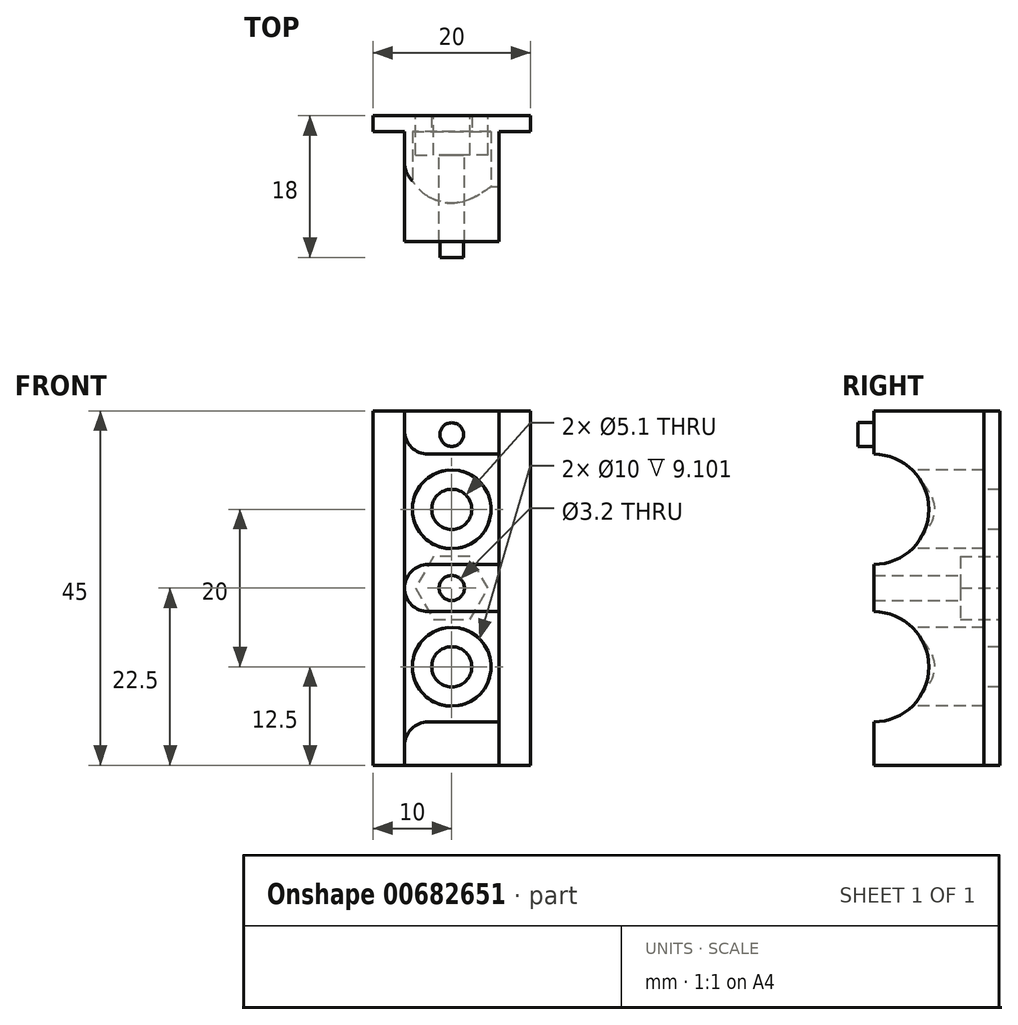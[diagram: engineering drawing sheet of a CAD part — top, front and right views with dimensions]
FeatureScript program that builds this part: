
annotation { "Feature Type Name" : "Feature", "Feature Type Description" : "" }
export const myFeature = defineFeature(function(context is Context, id is Id, definition is map)
    precondition{}
    {
        {
            var Q0;
            Q0=qCreatedBy(makeId("Front.planeOp"),FACE);
            cPlane(context, id + "F0", {"entities" : qUnion([Q0]), "cplaneType" : CPlaneType.OFFSET, "offset" : 16 * mm, "width" : 150 * mm, "height" : 150 * mm});
        }
        {
            var Q0;
            Q0=qCreatedBy(makeId("Front.planeOp"),FACE);
            var sketch = newSketch(context, id + "F1", { "sketchPlane" : qUnion([Q0])});
            skLineSegment(sketch, "E0.bottom", {"start": v(-6, 22.5) * mm, "end": v(6, 22.5) * mm});
            skLineSegment(sketch, "E0.top", {"start": v(-6, -22.5) * mm, "end": v(6, -22.5) * mm});
            skLineSegment(sketch, "E0.left", {"start": v(-6, 22.5) * mm, "end": v(-6, -22.5) * mm});
            skLineSegment(sketch, "E0.right", {"start": v(6, 22.5) * mm, "end": v(6, -22.5) * mm});
            skSolve(sketch);
        }
        {
            var Q0;
            Q0=qSketchRegion(id+"F1",true);
            extrude(context, id + "F2", {"entities" : qUnion([Q0]), "depth" : 30 * mm, "offsetDistance" : 25 * mm});
        }
        {
            var Q0;
            Q0=makeQuery(id+"F2.opExtrude","SWEPT_FACE",FACE,{"disambiguationData":[OSD([sQuery(id+"F1.wireOp",EDGE,"E0.right")])]});
            var sketch = newSketch(context, id + "F3", { "sketchPlane" : qUnion([Q0])});
            skCircle(sketch, "E1", {"center": v(-16, 10) * mm, "radius": 7 * mm});
            skCircle(sketch, "E2", {"center": v(-16, -10) * mm, "radius": 7 * mm});
            skSolve(sketch);
        }
        {
            var Q0;
            Q0=qSketchRegion(id+"F3",true);
            extrude(context, id + "F4", {"entities" : qUnion([Q0]), "operationType" : NewBodyOperationType.REMOVE, "endBound" : BoundingType.THROUGH_ALL, "oppositeDirection" : true, "depth" : 25 * mm, "offsetDistance" : 25 * mm});
        }
        {
            var Q0;
            Q0=qCreatedBy(makeId("Front.planeOp"),FACE);
            var sketch = newSketch(context, id + "F5", { "sketchPlane" : qUnion([Q0])});
            skLineSegment(sketch, "E3.bottom", {"start": v(-10, 22.5) * mm, "end": v(10, 22.5) * mm});
            skLineSegment(sketch, "E3.top", {"start": v(-10, -22.5) * mm, "end": v(10, -22.5) * mm});
            skLineSegment(sketch, "E3.left", {"start": v(-10, 22.5) * mm, "end": v(-10, -22.5) * mm});
            skLineSegment(sketch, "E3.right", {"start": v(10, 22.5) * mm, "end": v(10, -22.5) * mm});
            skPoint(sketch, "E4", {"position": v(0, 22.5) * mm});
            skSolve(sketch);
        }
        {
            var Q0;
            Q0=qSketchRegion(id+"F5",true);
            extrude(context, id + "F6", {"entities" : qUnion([Q0]), "operationType" : NewBodyOperationType.ADD, "depth" : 2 * mm, "offsetDistance" : 25 * mm});
        }
        {
            var Q0;
            Q0=makeQuery(id+"F4.boolean.opBoolean","INTERSECT",EDGE,{"derivedFrom":[makeQuery(id+"F2.opExtrude","SWEPT_FACE",FACE,{"disambiguationData":[OSD([sQuery(id+"F1.wireOp",EDGE,"E0.left")])]}),makeQuery(id+"F4.opExtrude","SWEPT_FACE",FACE,{"disambiguationData":[OSD([sQuery(id+"F3.wireOp",EDGE,"E1")])]})]});
            var Q1;
            Q1=makeQuery(id+"F4.boolean.opBoolean","INTERSECT",EDGE,{"derivedFrom":[makeQuery(id+"F2.opExtrude","SWEPT_FACE",FACE,{"disambiguationData":[OSD([sQuery(id+"F1.wireOp",EDGE,"E0.left")])]}),makeQuery(id+"F4.opExtrude","SWEPT_FACE",FACE,{"disambiguationData":[OSD([sQuery(id+"F3.wireOp",EDGE,"E2")])]})]});
            var Q2;
            Q2=makeQuery(id+"F4.boolean.opBoolean","COPY",EDGE,{"derivedFrom":makeQuery(id+"F4.opExtrude","CAP_EDGE",EDGE,{"disambiguationData":[OSD([sQuery(id+"F3.wireOp",EDGE,"E1")])],"isStart":true})});
            var Q3;
            Q3=makeQuery(id+"F4.boolean.opBoolean","COPY",EDGE,{"derivedFrom":makeQuery(id+"F4.opExtrude","CAP_EDGE",EDGE,{"disambiguationData":[OSD([sQuery(id+"F3.wireOp",EDGE,"E2")])],"isStart":true})});
            fillet(context, id + "F7", {"entities" : qUnion([Q0, Q1, Q2, Q3]), "radius" : 3 * mm, "tangentPropagation" : true, "allowEdgeOverflow" : false});
        }
        {
            var Q0;
            Q0=makeQuery(id+"F6.boolean.opBoolean","MERGE",FACE,{"derivedFrom":[makeQuery(id+"F2.opExtrude","CAP_FACE",FACE,{"disambiguationData":[OSD([sQuery(id+"F1.wireOp",EDGE,"E0.bottom"),sQuery(id+"F1.wireOp",EDGE,"E0.top"),sQuery(id+"F1.wireOp",EDGE,"E0.left"),sQuery(id+"F1.wireOp",EDGE,"E0.right")])],"isStart":true}),makeQuery(id+"F6.opExtrude","CAP_FACE",FACE,{"disambiguationData":[OSD([sQuery(id+"F5.wireOp",EDGE,"E3.bottom"),sQuery(id+"F5.wireOp",EDGE,"E3.top"),sQuery(id+"F5.wireOp",EDGE,"E3.left"),sQuery(id+"F5.wireOp",EDGE,"E3.right")])],"isStart":true})]});
            var sketch = newSketch(context, id + "F8", { "sketchPlane" : qUnion([Q0])});
            skPoint(sketch, "E5", {"position": v(0, 10) * mm});
            skPoint(sketch, "E6", {"position": v(0, -10) * mm});
            skPoint(sketch, "E7", {"position": v(0, 0) * mm});
            skSolve(sketch);
        }
        {
            var Q0;
            Q0=sQuery(id+"F8.wireOp",VERTEX,"E5");
            var Q1;
            Q1=sQuery(id+"F8.wireOp",VERTEX,"E6");
            var Q2;
            Q2=sQuery(id+"F8.wireOp",VERTEX,"E7");
            var Q3;
            Q3=makeQuery(id+"F2.opExtrude","SWEPT_BODY",BODY,{"disambiguationData":[OSD([sQuery(id+"F1.wireOp",EDGE,"E0.bottom"),sQuery(id+"F1.wireOp",EDGE,"E0.top"),sQuery(id+"F1.wireOp",EDGE,"E0.left"),sQuery(id+"F1.wireOp",EDGE,"E0.right")])]});
            hole(context, id + "F9", {"style" : HoleStyle.SIMPLE, "endStyle" : HoleEndStyle.THROUGH, "holeDiameter" : 3.2 * mm, "majorDiameter" : 5 * mm, "isTappedThrough" : true, "tappedDepth" : 12 * mm, "tapClearance" : 3, "startFromSketch" : true, "locations" : qUnion([Q0, Q1, Q2]), "scope" : qUnion([Q3])});
        }
        {
            var Q0;
            Q0=makeQuery(id+"F6.boolean.opBoolean","MERGE",FACE,{"derivedFrom":[makeQuery(id+"F2.opExtrude","CAP_FACE",FACE,{"disambiguationData":[OSD([sQuery(id+"F1.wireOp",EDGE,"E0.bottom"),sQuery(id+"F1.wireOp",EDGE,"E0.top"),sQuery(id+"F1.wireOp",EDGE,"E0.left"),sQuery(id+"F1.wireOp",EDGE,"E0.right")])],"isStart":true}),makeQuery(id+"F6.opExtrude","CAP_FACE",FACE,{"disambiguationData":[OSD([sQuery(id+"F5.wireOp",EDGE,"E3.bottom"),sQuery(id+"F5.wireOp",EDGE,"E3.top"),sQuery(id+"F5.wireOp",EDGE,"E3.left"),sQuery(id+"F5.wireOp",EDGE,"E3.right")])],"isStart":true})]});
            var sketch = newSketch(context, id + "F10", { "sketchPlane" : qUnion([Q0])});
            skSolve(sketch);
        }
        {
            var Q0;
            Q0=makeQuery(id+"F2.opExtrude","CAP_EDGE",EDGE,{"disambiguationData":[OSD([sQuery(id+"F1.wireOp",EDGE,"E0.top")])],"isStart":false});
            var Q1;
            Q1=makeQuery(id+"F2.opExtrude","CAP_EDGE",EDGE,{"disambiguationData":[OSD([sQuery(id+"F1.wireOp",EDGE,"E0.bottom")])],"isStart":false});
            chamfer(context, id + "F11", {"entities" : qUnion([Q0, Q1]), "width" : 1 * mm, "tangentPropagation" : true});
        }
        {
            var Q0;
            Q0=qCreatedBy(id+"F0.planeOp",FACE);
            var sketch = newSketch(context, id + "F12", { "sketchPlane" : qUnion([Q0])});
            skPoint(sketch, "E8", {"position": v(0, 10) * mm});
            skPoint(sketch, "E9", {"position": v(0, -10) * mm});
            skSolve(sketch);
        }
        {
            var Q0;
            Q0=sQuery(id+"F12.wireOp",VERTEX,"E9");
            var Q1;
            Q1=sQuery(id+"F12.wireOp",VERTEX,"E8");
            var Q2;
            Q2=makeQuery(id+"F2.opExtrude","SWEPT_BODY",BODY,{"disambiguationData":[OSD([sQuery(id+"F1.wireOp",EDGE,"E0.bottom"),sQuery(id+"F1.wireOp",EDGE,"E0.top"),sQuery(id+"F1.wireOp",EDGE,"E0.left"),sQuery(id+"F1.wireOp",EDGE,"E0.right")])]});
            hole(context, id + "F13", {"style" : HoleStyle.C_BORE, "endStyle" : HoleEndStyle.THROUGH, "holeDiameter" : 5.1 * mm, "cBoreDiameter" : 10 * mm, "cBoreDepth" : 14 * mm, "majorDiameter" : 5 * mm, "isTappedThrough" : true, "tappedDepth" : 12 * mm, "tapClearance" : 3, "startFromSketch" : true, "locations" : qUnion([Q0, Q1]), "scope" : qUnion([Q2])});
        }
        {
            var Q0;
            Q0=makeQuery(id+"F10.imprint","IMPRINT",FACE,{"disambiguationData":[TD([[makeQuery(id+"F10.imprint","IMPRINT",EDGE,{"derivedFrom":makeQuery(id+"F6.opExtrude","CAP_EDGE",EDGE,{"disambiguationData":[OSD([sQuery(id+"F5.wireOp",EDGE,"E3.left")])],"isStart":true})}),-1.0]])]});
            var sketch = newSketch(context, id + "F14", { "sketchPlane" : qUnion([Q0])});
            skCircle(sketch, "E10.cCircle", {"center": v(0, 0) * mm, "radius": 4 * mm, "construction": true});
            skLineSegment(sketch, "E10.0", {"start": v(4.62, 0) * mm, "end": v(2.3, -4) * mm});
            skLineSegment(sketch, "E10.1", {"start": v(2.3, -4) * mm, "end": v(-2.3, -4) * mm});
            skLineSegment(sketch, "E10.2", {"start": v(-2.3, -4) * mm, "end": v(-4.62, 0) * mm});
            skLineSegment(sketch, "E10.3", {"start": v(-4.62, 0) * mm, "end": v(-2.3, 4) * mm});
            skLineSegment(sketch, "E10.4", {"start": v(-2.3, 4) * mm, "end": v(2.3, 4) * mm});
            skLineSegment(sketch, "E10.5", {"start": v(2.3, 4) * mm, "end": v(4.62, 0) * mm});
            skPoint(sketch, "E10.0.midPoint", {"position": v(3.46, -2) * mm});
            skSolve(sketch);
        }
        {
            var Q0;
            Q0 = qSketchRegion(id + "F14", true);
            extrude(context, id + "F15", {"entities" : qUnion([Q0]), "operationType" : NewBodyOperationType.REMOVE, "oppositeDirection" : true, "depth" : 5 * mm, "offsetDistance" : 25 * mm});
        }
        {
            var Q0;
            Q0=qCreatedBy(id+"F0.planeOp",FACE);
            var sketch = newSketch(context, id + "F16", { "sketchPlane" : qUnion([Q0])});
            skLineSegment(sketch, "E11.bottom", {"start": v(-21.41, 33.65) * mm, "end": v(20.43, 33.65) * mm});
            skLineSegment(sketch, "E11.top", {"start": v(-21.41, -33.85) * mm, "end": v(20.43, -33.85) * mm});
            skLineSegment(sketch, "E11.left", {"start": v(-21.41, 33.65) * mm, "end": v(-21.41, -33.85) * mm});
            skLineSegment(sketch, "E11.right", {"start": v(20.43, 33.65) * mm, "end": v(20.43, -33.85) * mm});
            skSolve(sketch);
        }
        {
            var Q0;
            Q0=qSketchRegion(id+"F16",true);
            extrude(context, id + "F17", {"entities" : qUnion([Q0]), "operationType" : NewBodyOperationType.REMOVE, "depth" : 25 * mm, "offsetDistance" : 25 * mm});
        }
        {
            var Q0;
            Q0=makeQuery(id+"F17.boolean.opBoolean","COPY",FACE,{"disambiguationData":[TD([makeQuery(id+"F2.opExtrude","SWEPT_FACE",FACE,{"disambiguationData":[OSD([sQuery(id+"F1.wireOp",EDGE,"E0.top")])]})])],"derivedFrom":makeQuery(id+"F17.opExtrude","CAP_FACE",FACE,{"disambiguationData":[OSD([sQuery(id+"F16.wireOp",EDGE,"E11.bottom"),sQuery(id+"F16.wireOp",EDGE,"E11.top"),sQuery(id+"F16.wireOp",EDGE,"E11.left"),sQuery(id+"F16.wireOp",EDGE,"E11.right")])],"isStart":true})});
            var sketch = newSketch(context, id + "F18", { "sketchPlane" : qUnion([Q0])});
            skCircle(sketch, "E12", {"center": v(0, 19.5) * mm, "radius": 1.5 * mm});
            skSolve(sketch);
        }
        {
            var Q0;
            Q0 = qSketchRegion(id + "F18", true);
            extrude(context, id + "F19", {"entities" : qUnion([Q0]), "operationType" : NewBodyOperationType.ADD, "depth" : 2 * mm, "offsetDistance" : 25 * mm});
        }
    });
